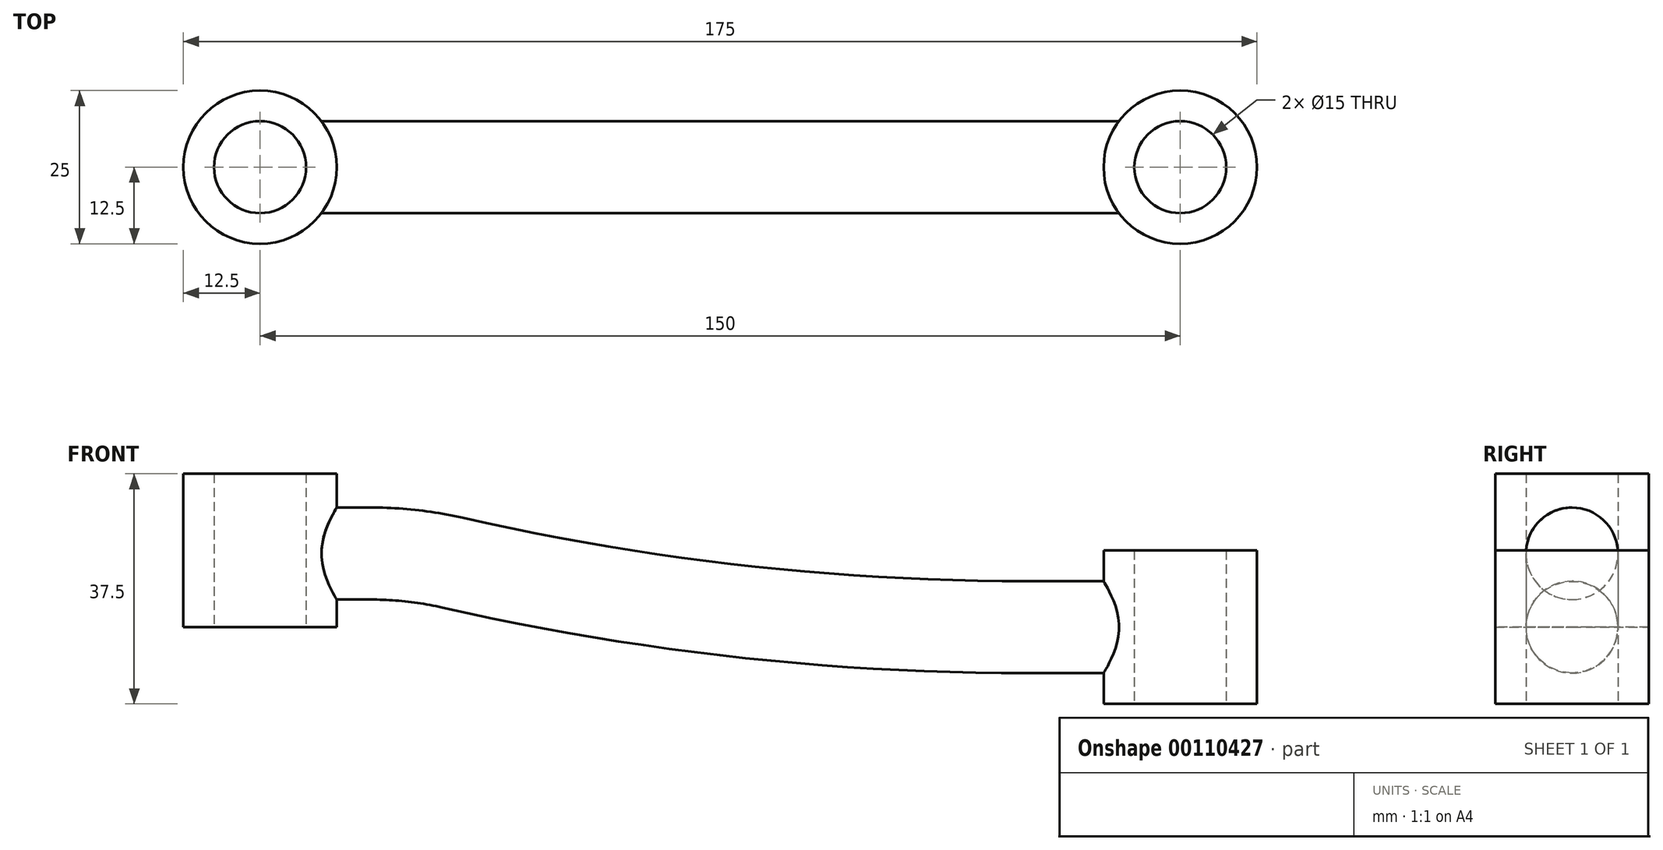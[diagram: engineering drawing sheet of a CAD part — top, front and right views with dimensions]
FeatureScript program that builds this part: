
annotation { "Feature Type Name" : "Feature", "Feature Type Description" : "" }
export const myFeature = defineFeature(function(context is Context, id is Id, definition is map)
    precondition{}
    {
        {
            var Q0;
            Q0=qCreatedBy(makeId("Front.planeOp"),FACE);
            var sketch = newSketch(context, id + "F0", { "sketchPlane" : qUnion([Q0])});
            skLineSegment(sketch, "E0", {"start": v(0, 12) * mm, "end": v(18.04, 12) * mm, "construction": true});
            skLineSegment(sketch, "E1", {"start": v(150, 0) * mm, "end": v(125, 0) * mm, "construction": true});
            skArc(sketch, "E2", {"start": v(125, 0) * mm, "mid": v(77.88, 2.64) * mm, "end": v(31.34, 10.5) * mm, "construction": true});
            skPoint(sketch, "E3.visualSharp", {"position": v(25, 12) * mm});
            skArc(sketch, "E3.filletArc", {"start": v(31.34, 10.5) * mm, "mid": v(24.73, 11.63) * mm, "end": v(18.04, 12) * mm, "construction": true});
            skLineSegment(sketch, "E4", {"start": v(150, 0) * mm, "end": v(125, 0) * mm});
            skLineSegment(sketch, "E5", {"start": v(0, 12) * mm, "end": v(18.04, 12) * mm});
            skArc(sketch, "E6", {"start": v(31.34, 10.5) * mm, "mid": v(24.73, 11.63) * mm, "end": v(18.04, 12) * mm});
            skArc(sketch, "E7", {"start": v(31.34, 10.5) * mm, "mid": v(77.88, 2.64) * mm, "end": v(125, 0) * mm});
            skSolve(sketch);
        }
        {
            var Q0;
            Q0=qCreatedBy(makeId("Right.planeOp"),FACE);
            var sketch = newSketch(context, id + "F1", { "sketchPlane" : qUnion([Q0])});
            skCircle(sketch, "E8", {"center": v(0, 12) * mm, "radius": 7.5 * mm});
            skSolve(sketch);
        }
        {
            var Q0;
            Q0 = qSketchRegion(id + "F1", true);
            var Q1;
            Q1 = qConstructionFilter(qBodyType(qCreatedBy(id + "F0" ,EDGE), BodyType.WIRE), ConstructionObject.NO);
            sweep(context, id + "F2", {"profiles" : qUnion([Q0]), "path" : qUnion([Q1])});
        }
        {
            var Q0;
            Q0=qCreatedBy(makeId("Top.planeOp"),FACE);
            var sketch = newSketch(context, id + "F3", { "sketchPlane" : qUnion([Q0])});
            skCircle(sketch, "E9", {"center": v(0, 0) * mm, "radius": 7.5 * mm});
            skCircle(sketch, "E10", {"center": v(0, 0) * mm, "radius": 12.5 * mm});
            skSolve(sketch);
        }
        {
            var Q0;
            Q0=makeQuery(id+"F3.imprint","IMPRINT",FACE,{"disambiguationData":[TD([[makeQuery(id+"F3.imprint","IMPRINT",EDGE,{"derivedFrom":sQuery(id+"F3.wireOp",EDGE,"E9")}),-1.0]])]});
            var Q1;
            Q1=makeQuery(id+"F3.imprint","IMPRINT",FACE,{"disambiguationData":[TD([[makeQuery(id+"F3.imprint","IMPRINT",EDGE,{"derivedFrom":sQuery(id+"F3.wireOp",EDGE,"E9")}),1.0]])]});
            extrude(context, id + "F4", {"entities" : qUnion([Q0, Q1]), "operationType" : NewBodyOperationType.ADD, "depth" : 25 * mm});
        }
        {
            var Q0;
            Q0=makeQuery(id+"F3.imprint","IMPRINT",FACE,{"disambiguationData":[TD([[makeQuery(id+"F3.imprint","IMPRINT",EDGE,{"derivedFrom":sQuery(id+"F3.wireOp",EDGE,"E9")}),1.0]])]});
            extrude(context, id + "F5", {"entities" : qUnion([Q0]), "operationType" : NewBodyOperationType.REMOVE, "endBound" : BoundingType.THROUGH_ALL, "depth" : 25 * mm});
        }
        {
            var Q0;
            Q0=makeQuery(id+"F2.opSweep","CAP_FACE",FACE,{"disambiguationData":[OSD([sQuery(id+"F0.wireOp",VERTEX,"E4.start"),sQuery(id+"F1.wireOp",EDGE,"E8")])],"isStart":false});
            var sketch = newSketch(context, id + "F6", { "sketchPlane" : qUnion([Q0])});
            skLineSegment(sketch, "E11", {"start": v(0, -13) * mm, "end": v(0, 12) * mm, "construction": true});
            skSolve(sketch);
        }
        {
            var Q0;
            Q0=qCreatedBy(makeId("Top.planeOp"),FACE);
            var sketch = newSketch(context, id + "F7", { "sketchPlane" : qUnion([Q0])});
            skCircle(sketch, "E12", {"center": v(150, 0) * mm, "radius": 12.5 * mm});
            skSolve(sketch);
        }
        {
            var Q0;
            Q0=makeQuery(id+"F7.imprint","IMPRINT",FACE,{"disambiguationData":[TD([[makeQuery(id+"F7.imprint","IMPRINT",EDGE,{"derivedFrom":sQuery(id+"F7.wireOp",EDGE,"E12")}),1.0]])]});
            extrude(context, id + "F8", {"entities" : qUnion([Q0]), "operationType" : NewBodyOperationType.ADD, "endBound" : BoundingType.SYMMETRIC, "depth" : 25 * mm});
        }
        {
            var Q0;
            Q0=makeQuery(id+"F8.opExtrude","CAP_FACE",FACE,{"disambiguationData":[OSD([sQuery(id+"F7.wireOp",EDGE,"E12")])],"isStart":true});
            var sketch = newSketch(context, id + "F9", { "sketchPlane" : qUnion([Q0])});
            skCircle(sketch, "E13", {"center": v(150, 0) * mm, "radius": 7.5 * mm});
            skSolve(sketch);
        }
        {
            var Q0;
            Q0=makeQuery(id+"F9.imprint","IMPRINT",FACE,{"disambiguationData":[TD([[makeQuery(id+"F9.imprint","IMPRINT",EDGE,{"derivedFrom":sQuery(id+"F9.wireOp",EDGE,"E13")}),1.0]])]});
            extrude(context, id + "F10", {"entities" : qUnion([Q0]), "operationType" : NewBodyOperationType.REMOVE, "endBound" : BoundingType.THROUGH_ALL, "oppositeDirection" : true, "depth" : 25 * mm});
        }
    });
